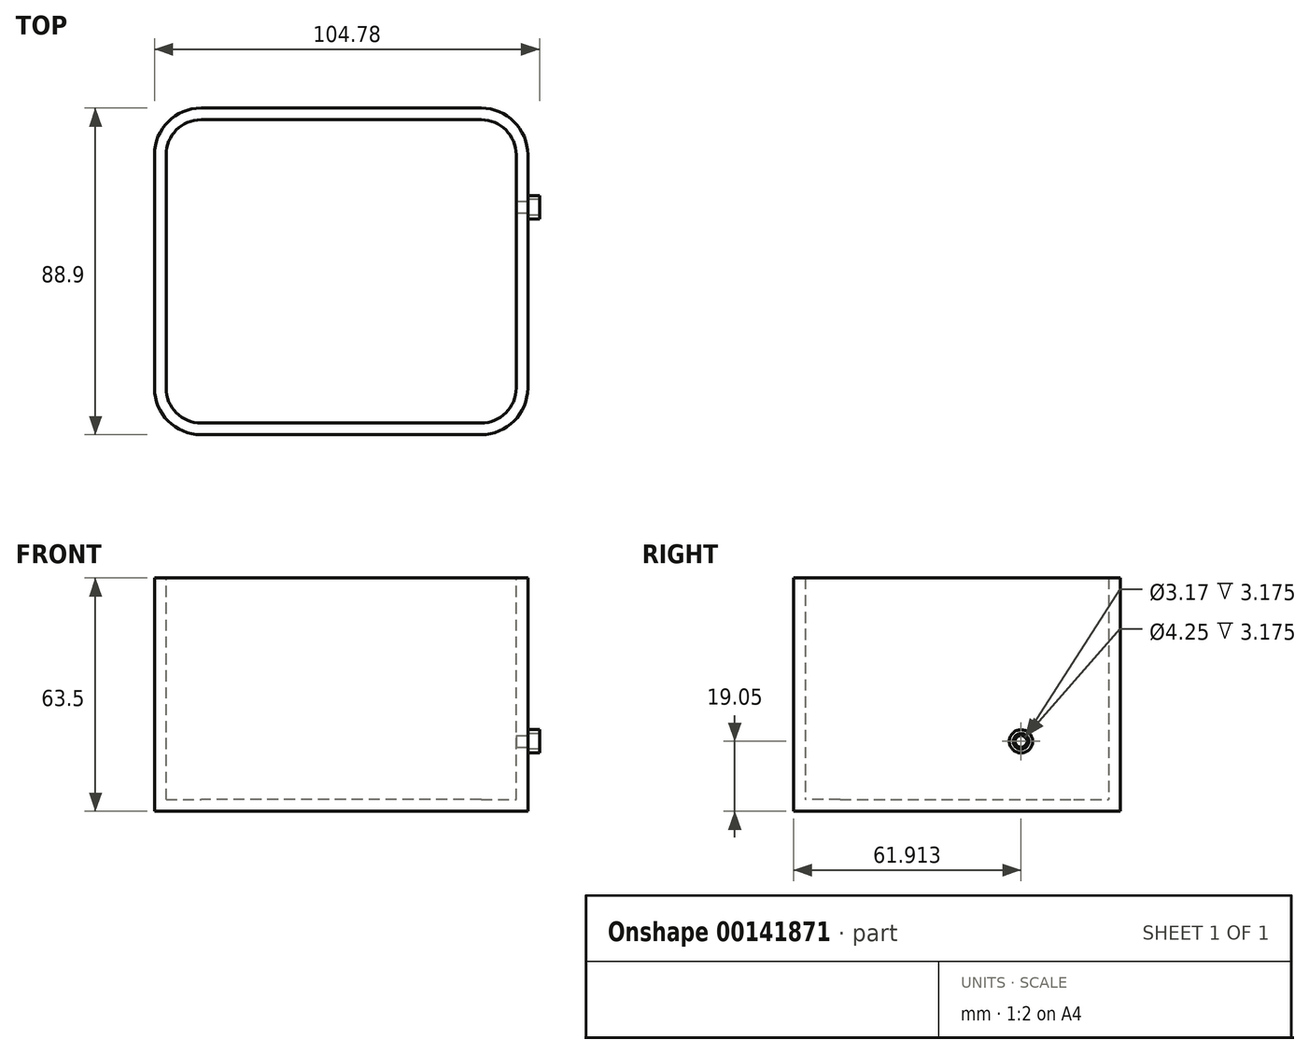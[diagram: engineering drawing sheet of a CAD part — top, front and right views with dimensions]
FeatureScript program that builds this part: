
annotation { "Feature Type Name" : "Feature", "Feature Type Description" : "" }
export const myFeature = defineFeature(function(context is Context, id is Id, definition is map)
    precondition{}
    {
        {
            var Q0;
            Q0=qCreatedBy(makeId("Top.planeOp"),FACE);
            var sketch = newSketch(context, id + "F5", { "sketchPlane" : qUnion([Q0])});
            skLineSegment(sketch, "E0.bottom", {"start": v(50.8, -44.45) * mm, "end": v(-50.8, -44.45) * mm});
            skLineSegment(sketch, "E0.top", {"start": v(50.8, 44.45) * mm, "end": v(-50.8, 44.45) * mm});
            skLineSegment(sketch, "E0.left", {"start": v(50.8, -44.45) * mm, "end": v(50.8, 44.45) * mm});
            skLineSegment(sketch, "E0.right", {"start": v(-50.8, -44.45) * mm, "end": v(-50.8, 44.45) * mm});
            skPoint(sketch, "E0.middle", {"position": v(0, 0) * mm});
            skSolve(sketch);
        }
        {
            var Q0;
            Q0=makeQuery(id+"F5.imprint","IMPRINT",FACE,{"disambiguationData":[TD([[makeQuery(id+"F5.imprint","IMPRINT",EDGE,{"derivedFrom":sQuery(id+"F5.wireOp",EDGE,"E0.bottom")}),-1.0]])]});
            extrude(context, id + "F6", {"entities" : qUnion([Q0]), "depth" : 63.5 * mm});
        }
        {
            var Q0;
            Q0=makeQuery(id+"F6.opExtrude","SWEPT_EDGE",EDGE,{"disambiguationData":[OSD([sQuery(id+"F5.wireOp",EDGE,"E0.bottom"),sQuery(id+"F5.wireOp",EDGE,"E0.left")])]});
            var Q1;
            Q1=makeQuery(id+"F6.opExtrude","SWEPT_EDGE",EDGE,{"disambiguationData":[OSD([sQuery(id+"F5.wireOp",EDGE,"E0.top"),sQuery(id+"F5.wireOp",EDGE,"E0.left")])]});
            var Q2;
            Q2=makeQuery(id+"F6.opExtrude","SWEPT_EDGE",EDGE,{"disambiguationData":[OSD([sQuery(id+"F5.wireOp",EDGE,"E0.bottom"),sQuery(id+"F5.wireOp",EDGE,"E0.right")])]});
            var Q3;
            Q3=makeQuery(id+"F6.opExtrude","SWEPT_EDGE",EDGE,{"disambiguationData":[OSD([sQuery(id+"F5.wireOp",EDGE,"E0.top"),sQuery(id+"F5.wireOp",EDGE,"E0.right")])]});
            fillet(context, id + "F0", {"entities" : qUnion([Q0, Q1, Q2, Q3]), "radius" : 12.7 * mm, "tangentPropagation" : true, "allowEdgeOverflow" : false});
        }
        {
            var Q0;
            Q0=makeQuery(id+"F6.opExtrude","CAP_FACE",FACE,{"disambiguationData":[OSD([sQuery(id+"F5.wireOp",EDGE,"E0.bottom"),sQuery(id+"F5.wireOp",EDGE,"E0.top"),sQuery(id+"F5.wireOp",EDGE,"E0.left"),sQuery(id+"F5.wireOp",EDGE,"E0.right")])],"isStart":false});
            shell(context, id + "F1", {"entities" : qUnion([Q0]), "thickness" : 3.17 * mm});
        }
        {
            var Q0;
            Q0=makeQuery(id+"F6.opExtrude","SWEPT_FACE",FACE,{"disambiguationData":[OSD([sQuery(id+"F5.wireOp",EDGE,"E0.left")])]});
            var sketch = newSketch(context, id + "F7", { "sketchPlane" : qUnion([Q0])});
            skPoint(sketch, "E1", {"position": v(17.46, 19.05) * mm});
            skSolve(sketch);
        }
        {
            var Q0;
            Q0=sQuery(id+"F7.wireOp",VERTEX,"E1");
            var Q1;
            Q1=makeQuery(id+"F6.opExtrude","SWEPT_BODY",BODY,{"disambiguationData":[OSD([sQuery(id+"F5.wireOp",EDGE,"E0.bottom"),sQuery(id+"F5.wireOp",EDGE,"E0.top"),sQuery(id+"F5.wireOp",EDGE,"E0.left"),sQuery(id+"F5.wireOp",EDGE,"E0.right")])]});
            hole(context, id + "F2", {"style" : HoleStyle.SIMPLE, "endStyle" : HoleEndStyle.BLIND, "holeDiameter" : 3.17 * mm, "holeDepth" : 12.7 * mm, "locations" : qUnion([Q0]), "scope" : qUnion([Q1])});
        }
        {
            var Q0;
            {var subQ0=sQuery(id+"F5.wireOp",EDGE,"E0.left");Q0=makeQuery(id+"F7.imprint","IMPRINT",FACE,{"disambiguationData":[TD([[makeQuery(id+"F7.imprint","IMPRINT",EDGE,{"derivedFrom":makeQuery(id+"F6.opExtrude","CAP_EDGE",EDGE,{"disambiguationData":[OSD([subQ0])],"isStart":true})}),1.0]])]});}
            var sketch = newSketch(context, id + "F3", { "sketchPlane" : qUnion([Q0])});
            skCircle(sketch, "E2", {"center": v(17.46, 19.05) * mm, "radius": 3.18 * mm});
            skCircle(sketch, "E3", {"center": v(17.46, 19.05) * mm, "radius": 2.13 * mm});
            skSolve(sketch);
        }
        {
            var Q0;
            Q0 = qSketchRegion(id + "F3", true);
            extrude(context, id + "F4", {"entities" : qUnion([Q0]), "operationType" : NewBodyOperationType.ADD, "depth" : 3.17 * mm});
        }
    });
